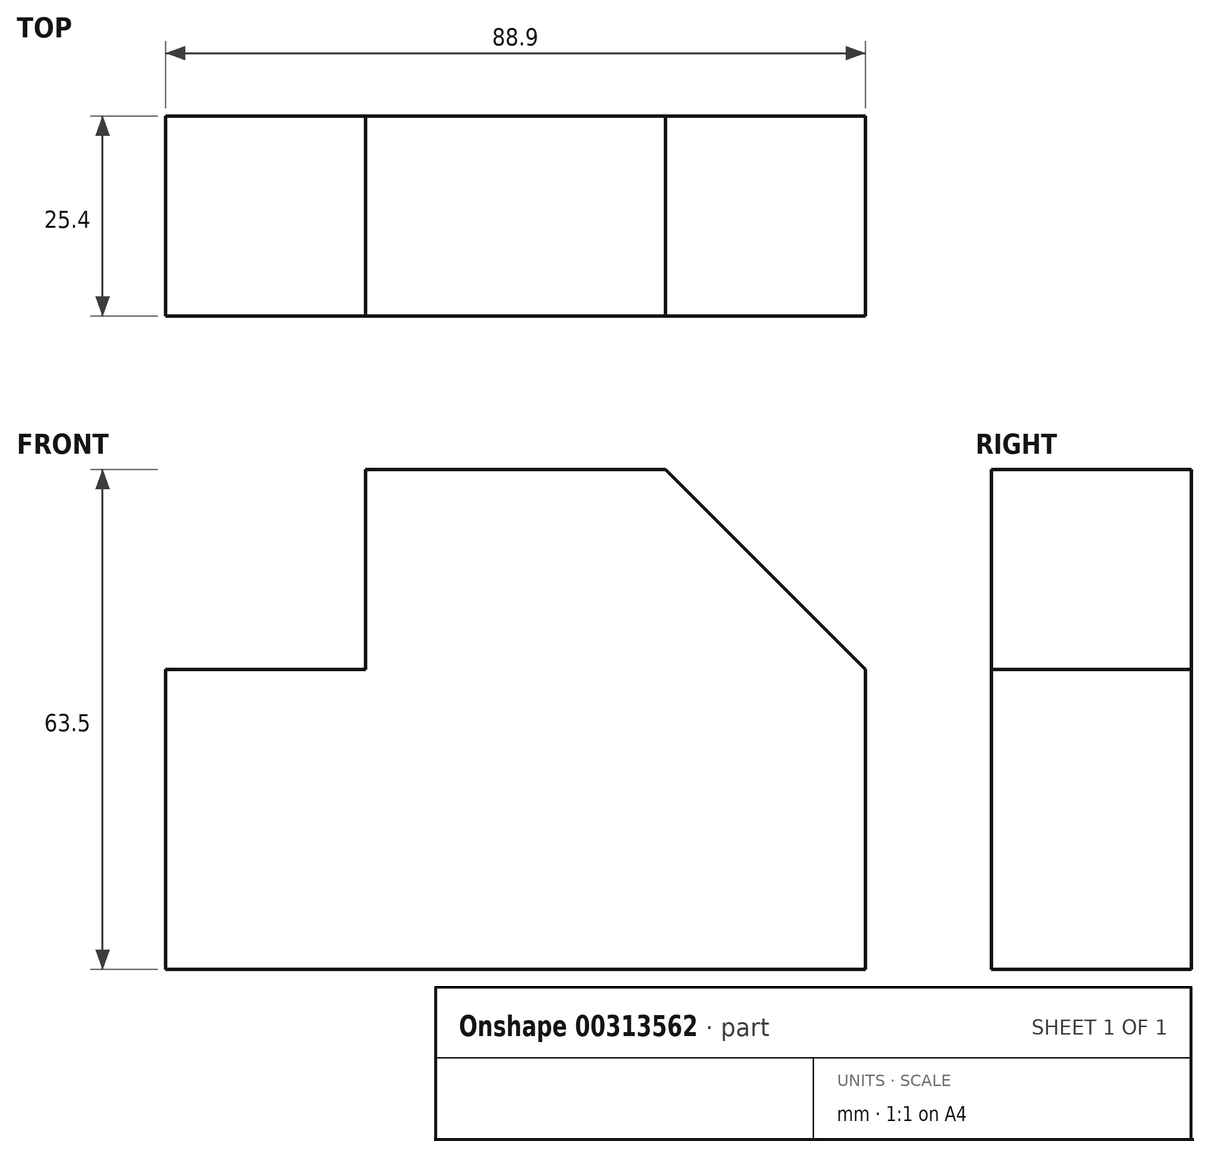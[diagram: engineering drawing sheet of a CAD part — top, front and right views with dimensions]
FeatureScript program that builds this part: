
annotation { "Feature Type Name" : "Feature", "Feature Type Description" : "" }
export const myFeature = defineFeature(function(context is Context, id is Id, definition is map)
    precondition{}
    {
        {
            var Q0;
            Q0=qCreatedBy(makeId("Front.planeOp"),FACE);
            var sketch = newSketch(context, id + "F0", { "sketchPlane" : qUnion([Q0])});
            skLineSegment(sketch, "E0", {"start": v(-34.7, -46.58) * mm, "end": v(54.2, -46.58) * mm});
            skLineSegment(sketch, "E1", {"start": v(54.2, -46.58) * mm, "end": v(54.2, -8.48) * mm});
            skLineSegment(sketch, "E2", {"start": v(-34.7, -46.58) * mm, "end": v(-34.7, -8.48) * mm});
            skLineSegment(sketch, "E3", {"start": v(-34.7, -8.48) * mm, "end": v(-9.3, -8.48) * mm});
            skLineSegment(sketch, "E4", {"start": v(-9.3, -8.48) * mm, "end": v(-9.3, 16.92) * mm});
            skLineSegment(sketch, "E5", {"start": v(-9.3, 16.92) * mm, "end": v(28.8, 16.92) * mm});
            skLineSegment(sketch, "E6", {"start": v(28.8, 16.92) * mm, "end": v(54.2, -8.48) * mm});
            skSolve(sketch);
        }
        {
            var Q0;
            Q0 = qSketchRegion(id + "F0", true);
            extrude(context, id + "F1", {"entities" : qUnion([Q0]), "depth" : 25.4 * mm});
        }
    });
